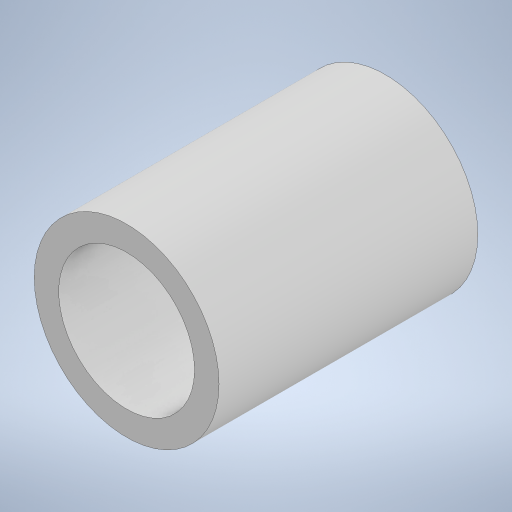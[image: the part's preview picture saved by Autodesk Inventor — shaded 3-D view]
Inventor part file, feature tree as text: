
AUTODESK INVENTOR PART (.ipt)
format: ipt  version: 2023 (Build 270158000, 158)  size: 206,336 bytes
history: native  units: mm
features: extrude x1, sketch x1
ambient origin geometry x8: Origin, YZ Plane, XZ Plane, XY Plane, X Axis, Y Axis, Z Axis, Center Point
bodies: Solid1 (feature_tree)
feature tree (2):
  extrude  "Extrusion1"  Depth=10.0mm
  sketch  "Sketch1"  dims[d0=7.35mm d1=10.0mm d2=14.0mm d3=0.0mm]
